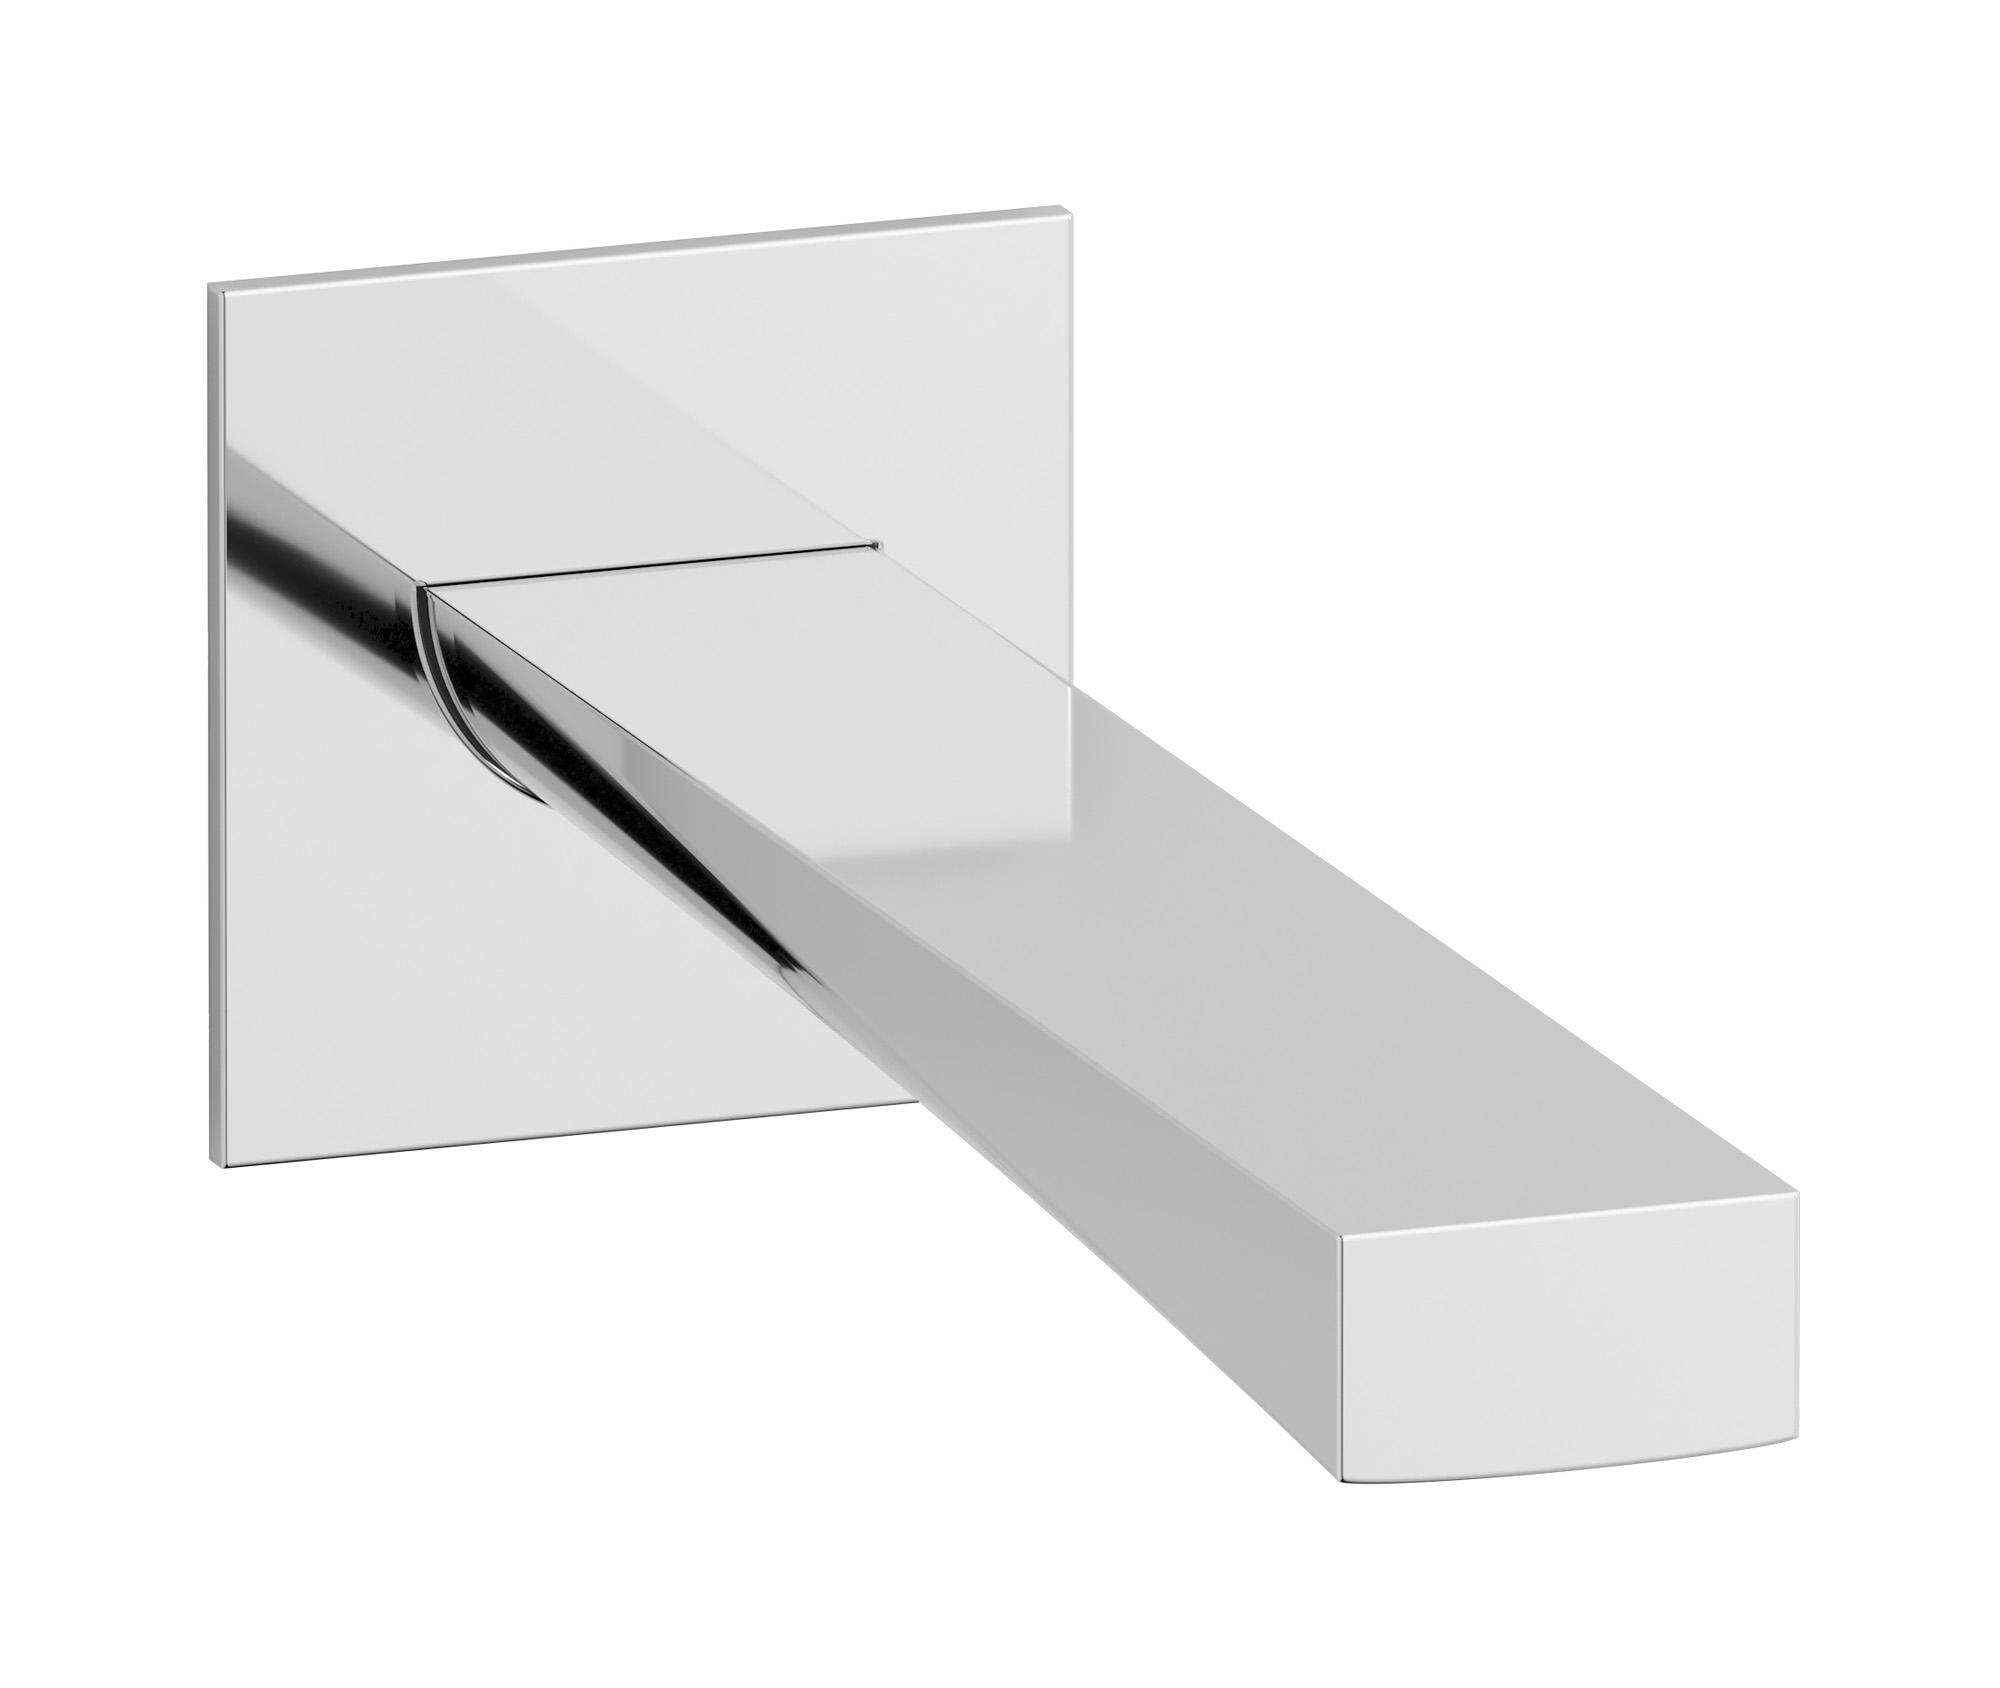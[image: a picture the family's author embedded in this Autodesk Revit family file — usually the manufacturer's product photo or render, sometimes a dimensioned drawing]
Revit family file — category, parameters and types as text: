
# Revit family: WA320
name_source: partatom
category: Apparecchi idraulici
units: mm (PartAtom-declared; Revit-internal decimal feet)

## family parameters
Basato su piano di lavoro = No
Condiviso = No
Mantieni orientamento annotazione = No
Numero OmniClass = 23.45.55.17
Punto di calcolo locali = No
Quota connettore circolare = Usa diametro
Sempre verticale = Sì
Taglio con vuoti quando caricato = No
Tipo di parte = Normale
Titolo OmniClass = Mixing Faucets

## types (12) — shared parameters
Commenti sul tipo = Wall mounted spout
Connessione CW = No
Connessione HW = No
Connessione di scarico = No
Connessione di ventilazione = No
Descrizione = Wall mounted spout
Produttore = IB Rubinetterie s.p.A.
URL = https://www.weareib.it
Water inlet = 10 mm  [stored 0.0328084 ft]
zero-valued in all types: Prospetto di default

## per-type parameters (varying)
| type | Finishes surface | Immagine tipo | Modello |
| Chrome | IB_Chrome | WA320CC.jpg | WA320CC |
| Brushed nickel | IB_Brushed nickel | WA320SS.jpg | WA320SS |
| Matt white | IB_matt white | WA320BO.jpg | WA320BO |
| Matt black | IB_matt black | WA320NP.jpg | WA320NP |
| Black chrome | IB_Black chrome | WA320CF.jpg | WA320CF |
| Brushed black chrome | IB_Brushed black chrome | WA320CS.jpg | WA320CS |
| Pale gold | IB_Pale gold | WA320II.jpg | WA320II |
| Brushed pale gold | IB_brushed pale gold | WA320IS.jpg | WA320IS |
| Rose gold | IB_Rose gold | WA320RS.jpg | WA320RS |
| Brushed rose gold | IB_Brushed rose gold | WA320SR.jpg | WA320SR |
| Gold | IB_gold | WA320OO.jpg | WA320OO |
| Brushed gold | IB_brushed gold | WA320OS.jpg | WA320OS |

note: [stored X ft] marks values corroborated as IEEE doubles in the binary element streams (Revit-internal decimal feet)
